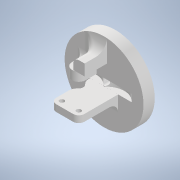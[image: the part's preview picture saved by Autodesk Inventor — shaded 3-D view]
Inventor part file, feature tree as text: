
AUTODESK INVENTOR PART (.ipt)
format: ipt  version: 2021 (Build 250183000, 183)  size: 308,736 bytes
history: native  units: mm
features: extrude x11, sketch x11, fillet x6, other x5, reference x2, projected_geometry x1
ambient origin geometry x8: Origin, YZ Plane, XZ Plane, XY Plane, X Axis, Y Axis, Z Axis, Center Point
bodies: Solid1 (feature_tree)
feature tree (36):
  extrude  "Extrusion1"  Depth=10.0mm TaperAngle=0.0deg
  extrude  "Extrusion2"  Depth=3.6mm TaperAngle=0.0deg
  extrude  "Extrusion3"  Depth=3.6mm TaperAngle=0.0deg
  extrude  "Extrusion4"  Depth=39.0mm
  fillet  "Fillet1"  Radius=2.7mm
  fillet  "Fillet2"  Radius=3.0mm
  extrude  "Extrusion5"  Depth=10.0mm
  extrude  "Extrusion6"  Depth=20.0mm TaperAngle=0.0deg
  extrude  "Extrusion7"  Depth=10.0mm
  fillet  "Fillet3"  Radius=20.0mm
  extrude  "Extrusion8"  Depth=8.0mm
  extrude  "Extrusion9"  Depth=3.6mm
  extrude  "Extrusion10"  Depth=10.0mm
  fillet  "Fillet4"  Radius=10.0mm
  fillet  "Fillet5"  Radius=5.0mm
  extrude  "Extrusion11"  Depth=10.0mm
  fillet  "Fillet6"  Radius=3.0mm
  sketch  "Sketch1"  dims[d0=70.0mm d1=10.0mm d2=0.0mm]
  sketch  "Sketch2"  dims[d3=21.0mm d4=3.6mm d5=0.0mm]
  sketch  "Sketch3"  dims[d6=6.0mm d7=3.6mm d8=0.0mm]
  sketch  "Sketch4"  dims[d9=40.5mm d10=39.0mm d11=2.7mm d12=3.0mm]
  sketch  "Sketch5"  dims[d13=10.0mm d14=10.0mm]
  sketch  "Sketch6"  dims[d15=12.5mm d16=20.0mm d17=0.0mm]
  reference  "Reference1"
  sketch  "Sketch7"  dims[d18=10.0mm d19=5.0mm d20=20.0mm]
  projected_geometry  "Projected Loop1"
  sketch  "Sketch8"  dims[d21=8.0mm d22=3.0mm]
  sketch  "Sketch9"  dims[d23=20.0mm d24=0.0mm d25=3.6mm]
  sketch  "Sketch10"  dims[d26=10.0mm d27=0.0mm d28=12.0mm d29=10.0mm d30=0.0mm d31=5.0mm]
  sketch  "Sketch11"  dims[d32=31.0mm d33=20.0mm d35=25.0mm d36=10.0mm d38=10.0mm d40=3.0mm d41=3.4mm d42=0.0mm d43=0.0mm d44=25.0mm d45=6.0mm d46=12.5mm d47=35.0mm d48=0.0mm d49=4.0mm d50=4.0mm d51=5.0mm d52=5.0mm d53=5.0mm d54=5.0mm d55=45.0mm d56=0.0mm d57=5.0mm d58=8.0mm d59=8.0mm d60=1.0mm d61=0.0mm d62=6.0mm d63=0.0mm d64=8.0mm d65=0.5mm d66=0.872665mm d67=0.5mm d68=0.872665mm]
  reference  "Reference2"
  parser-record x1  (decoder bookkeeping rows leaked as tree rows — omitted from the tree; the rows remain in map.json)
  other  "Złożenie gripper.iam"
  other  "przekładnia gripper:1"
  other  "Spur Gears:1"
  other  "Spur Gear2:1"
note: 1 file-system path scrubbed to <path> (originals preserved in map.json)
